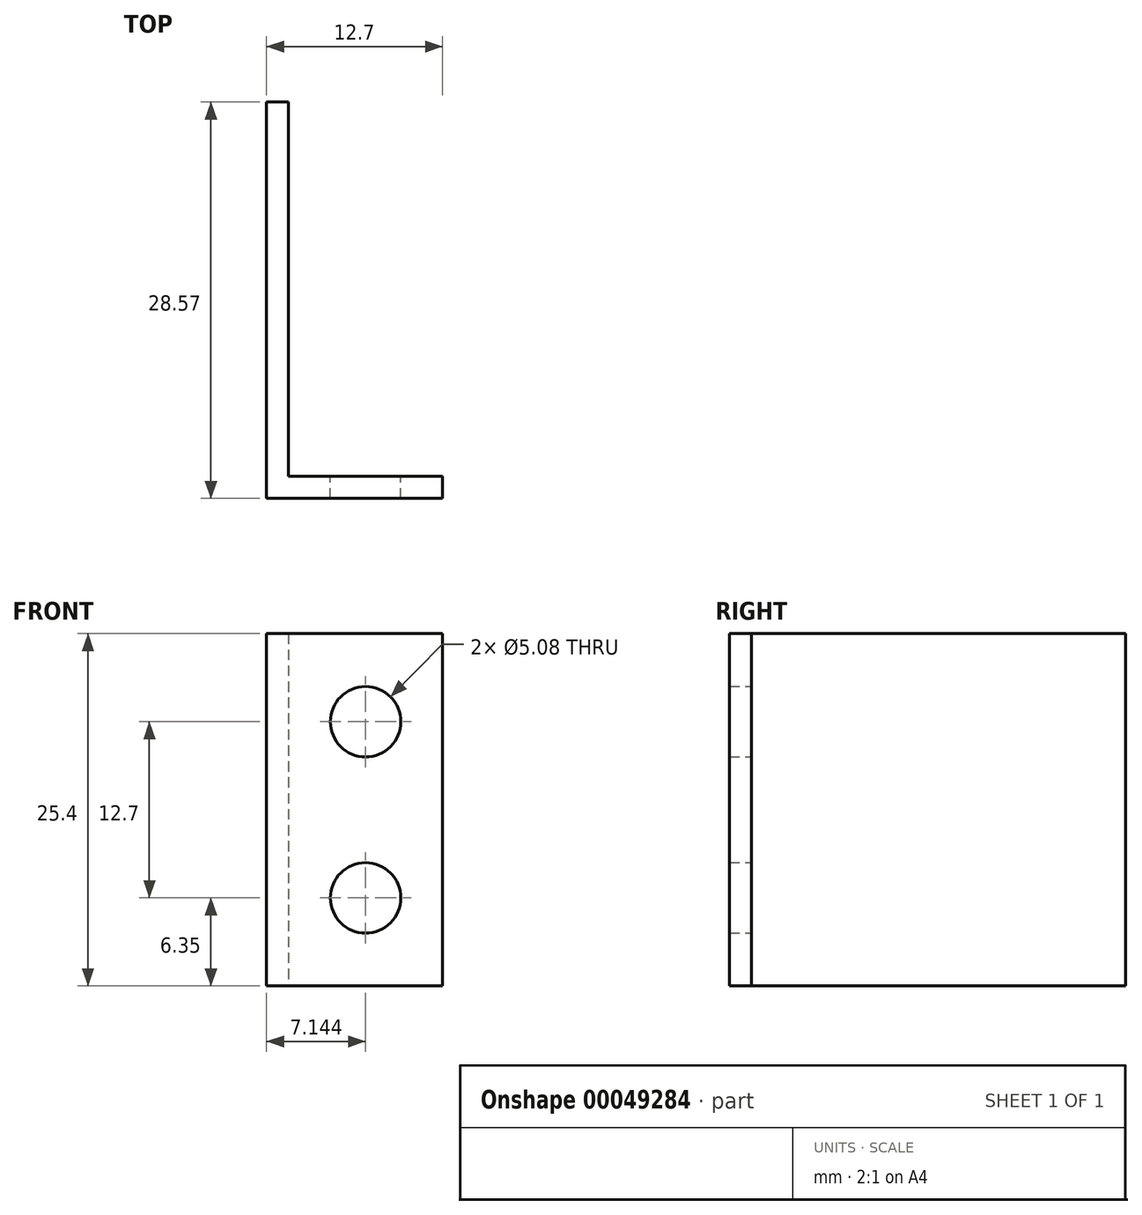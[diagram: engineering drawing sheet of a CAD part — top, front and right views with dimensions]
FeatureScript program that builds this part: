
annotation { "Feature Type Name" : "Feature", "Feature Type Description" : "" }
export const myFeature = defineFeature(function(context is Context, id is Id, definition is map)
    precondition{}
    {
        {
            var Q0;
            Q0=qCreatedBy(makeId("Top.planeOp"),FACE);
            var sketch = newSketch(context, id + "F0", { "sketchPlane" : qUnion([Q0])});
            skLineSegment(sketch, "E0", {"start": v(0, 0) * mm, "end": v(0, 28.58) * mm});
            skLineSegment(sketch, "E1", {"start": v(0, 0) * mm, "end": v(12.7, 0) * mm});
            skLineSegment(sketch, "E2.0", {"start": v(1.59, 1.59) * mm, "end": v(1.59, 28.58) * mm});
            skLineSegment(sketch, "E2.1", {"start": v(1.59, 1.59) * mm, "end": v(12.7, 1.59) * mm});
            skLineSegment(sketch, "E3", {"start": v(0, 28.58) * mm, "end": v(1.59, 28.58) * mm});
            skLineSegment(sketch, "E4", {"start": v(12.7, 1.59) * mm, "end": v(12.7, 0) * mm});
            skSolve(sketch);
        }
        {
            var Q0;
            Q0 = qSketchRegion(id + "F0", true);
            extrude(context, id + "F1", {"entities" : qUnion([Q0]), "depth" : 25.4 * mm});
        }
        {
            var Q0;
            Q0=makeQuery(id+"F1.opExtrude","SWEPT_FACE",FACE,{"disambiguationData":[OSD([sQuery(id+"F0.wireOp",EDGE,"E2.1")])]});
            var sketch = newSketch(context, id + "F2", { "sketchPlane" : qUnion([Q0])});
            skLineSegment(sketch, "E5", {"start": v(-7.14, 25.4) * mm, "end": v(-7.14, 0) * mm, "construction": true});
            skLineSegment(sketch, "E6", {"start": v(-12.7, 12.7) * mm, "end": v(-1.59, 12.7) * mm, "construction": true});
            skCircle(sketch, "E7", {"center": v(-7.14, 19.05) * mm, "radius": 2.54 * mm});
            skCircle(sketch, "E8.MirrorC", {"center": v(-7.14, 6.35) * mm, "radius": 2.54 * mm});
            skSolve(sketch);
        }
        {
            var Q0;
            Q0 = qSketchRegion(id + "F2", true);
            extrude(context, id + "F3", {"entities" : qUnion([Q0]), "operationType" : NewBodyOperationType.REMOVE, "endBound" : BoundingType.THROUGH_ALL, "oppositeDirection" : true, "depth" : 25.4 * mm});
        }
    });
